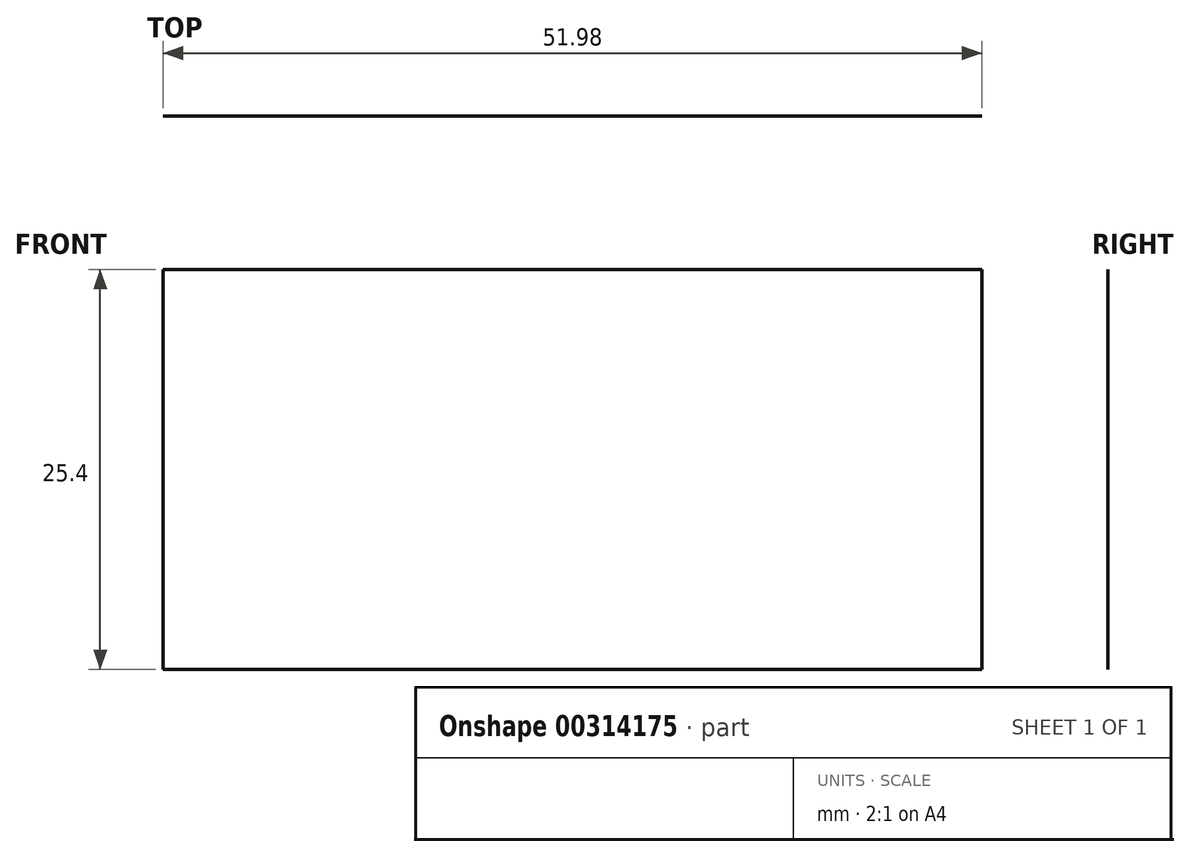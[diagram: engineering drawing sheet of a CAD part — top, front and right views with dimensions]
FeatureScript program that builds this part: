
annotation { "Feature Type Name" : "Feature", "Feature Type Description" : "" }
export const myFeature = defineFeature(function(context is Context, id is Id, definition is map)
    precondition{}
    {
        {
            var Q0;
            Q0=qCreatedBy(makeId("Top.planeOp"),FACE);
            var sketch = newSketch(context, id + "F0", { "sketchPlane" : qUnion([Q0])});
            skLineSegment(sketch, "E0", {"start": v(0, 0) * mm, "end": v(51.98, 0) * mm});
            skSolve(sketch);
        }
        {
            var Q0;
            Q0=sQuery(id+"F0.wireOp",EDGE,"E0");
            extrude(context, id + "F1", {"bodyType" : ToolBodyType.SURFACE, "surfaceEntities" : qUnion([Q0]), "depth" : 25.4 * mm});
        }
    });
